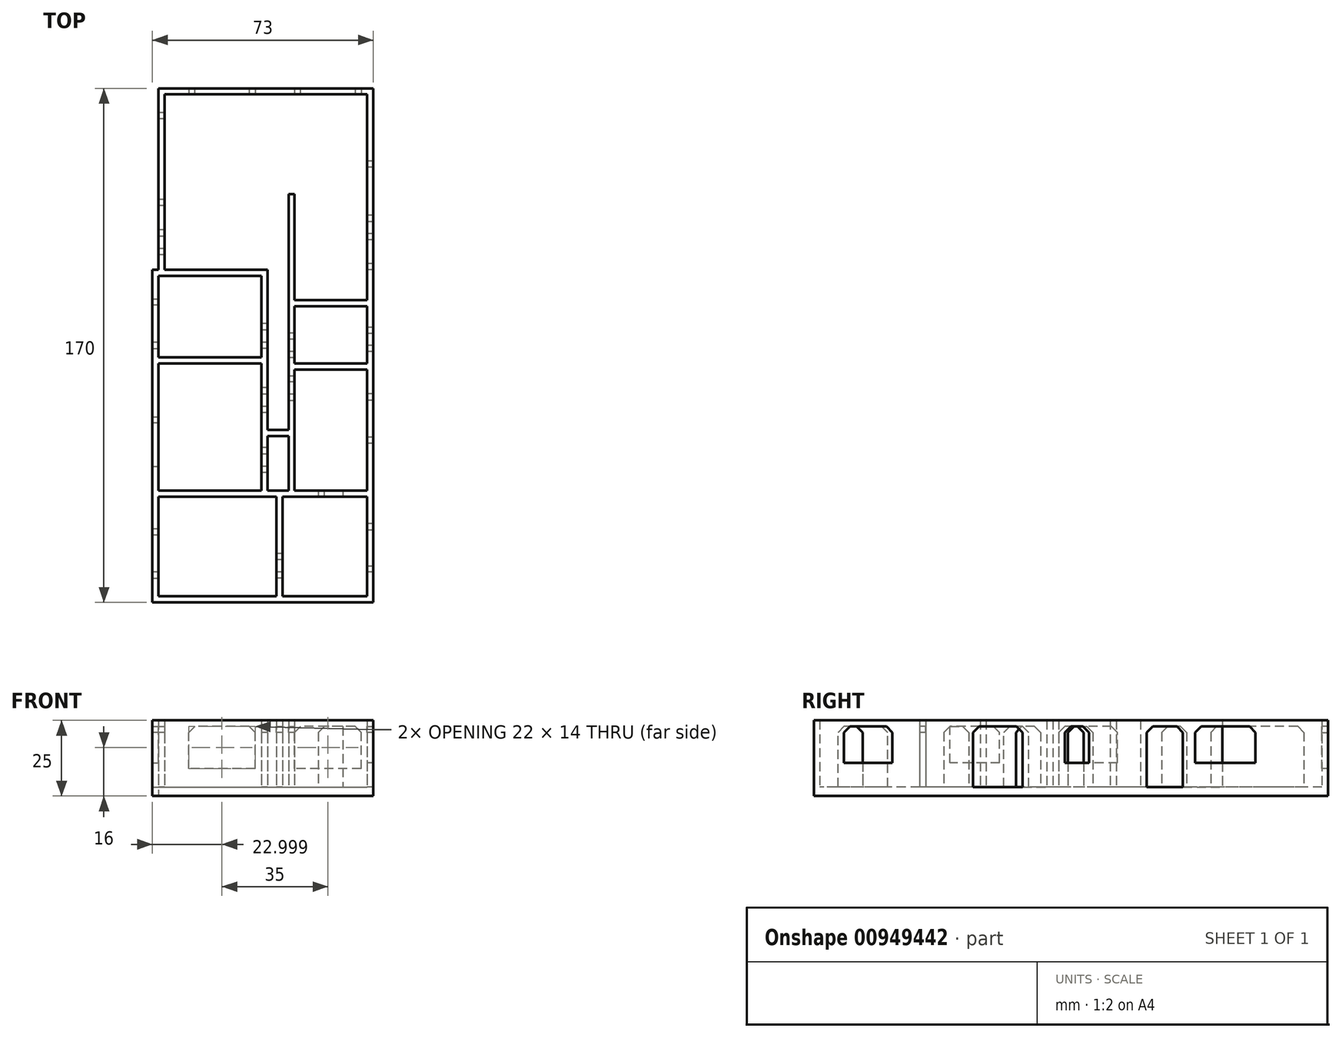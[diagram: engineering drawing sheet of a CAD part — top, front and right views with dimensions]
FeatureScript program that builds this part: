
annotation { "Feature Type Name" : "Feature", "Feature Type Description" : "" }
export const myFeature = defineFeature(function(context is Context, id is Id, definition is map)
    precondition{}
    {
        {
            assignVariable(context, id + "F0", {"name" : "WallWidth", "anyValue" : 2});
        }
        {
            assignVariable(context, id + "F1", {"name" : "Floor", "anyValue" : 3});
        }
        {
            assignVariable(context, id + "F2", {"name" : "DoorC", "anyValue" : 2});
        }
        {
            var Q0;
            Q0=qCreatedBy(makeId("Top.planeOp"),FACE);
            var sketch = newSketch(context, id + "F3", { "sketchPlane" : qUnion([Q0])});
            skLineSegment(sketch, "E0.bottom", {"start": v(-13.18, 167.27) * mm, "end": v(57.82, 167.27) * mm});
            skLineSegment(sketch, "E0.top", {"start": v(-13.18, -2.73) * mm, "end": v(57.82, -2.73) * mm});
            skLineSegment(sketch, "E0.left", {"start": v(-13.18, 167.27) * mm, "end": v(-13.18, -2.73) * mm});
            skLineSegment(sketch, "E0.right", {"start": v(57.82, 167.27) * mm, "end": v(57.82, -2.73) * mm});
            skLineSegment(sketch, "E1.bottom", {"start": v(-13.18, -2.73) * mm, "end": v(-15.18, -2.73) * mm});
            skLineSegment(sketch, "E1.top", {"start": v(-13.18, 107.27) * mm, "end": v(-15.18, 107.27) * mm});
            skLineSegment(sketch, "E1.left", {"start": v(-13.18, -2.73) * mm, "end": v(-13.18, 107.27) * mm});
            skLineSegment(sketch, "E1.right", {"start": v(-15.18, -2.73) * mm, "end": v(-15.18, 107.27) * mm});
            skSolve(sketch);
        }
        {
            var Q0;
            Q0 = qSketchRegion(id + "F3", true);
            extrude(context, id + "F4", {"entities" : qUnion([Q0]), "depth" : (getVariable(context, 'Floor')) * mm, "offsetDistance" : 25 * mm});
        }
        {
            var Q0;
            Q0=makeQuery(id+"F4.opExtrude","CAP_FACE",FACE,{"disambiguationData":[OSD([sQuery(id+"F3.wireOp",EDGE,"E0.bottom"),sQuery(id+"F3.wireOp",EDGE,"E0.top"),sQuery(id+"F3.wireOp",EDGE,"E0.left"),sQuery(id+"F3.wireOp",EDGE,"E0.right"),sQuery(id+"F3.wireOp",EDGE,"E1.bottom"),sQuery(id+"F3.wireOp",EDGE,"E1.top"),sQuery(id+"F3.wireOp",EDGE,"E1.right")])],"isStart":false});
            var sketch = newSketch(context, id + "F5", { "sketchPlane" : qUnion([Q0])});
            skLineSegment(sketch, "E2.bottom", {"start": v(-15.18, -2.73) * mm, "end": v(57.82, -2.73) * mm});
            skLineSegment(sketch, "E2.top", {"start": v(-15.18, -0.73) * mm, "end": v(57.82, -0.73) * mm});
            skLineSegment(sketch, "E2.left", {"start": v(-15.18, -2.73) * mm, "end": v(-15.18, -0.73) * mm});
            skLineSegment(sketch, "E2.right", {"start": v(57.82, -2.73) * mm, "end": v(57.82, -0.73) * mm});
            skLineSegment(sketch, "E3.bottom", {"start": v(25.82, 32.27) * mm, "end": v(27.82, 32.27) * mm});
            skLineSegment(sketch, "E3.top", {"start": v(25.82, -0.73) * mm, "end": v(27.82, -0.73) * mm});
            skLineSegment(sketch, "E3.left", {"start": v(25.82, 32.27) * mm, "end": v(25.82, -0.73) * mm});
            skLineSegment(sketch, "E3.right", {"start": v(27.82, 32.27) * mm, "end": v(27.82, -0.73) * mm});
            skLineSegment(sketch, "E4.bottom", {"start": v(-15.18, 107.27) * mm, "end": v(-13.18, 107.27) * mm});
            skLineSegment(sketch, "E4.top", {"start": v(-15.18, -0.73) * mm, "end": v(-13.18, -0.73) * mm});
            skLineSegment(sketch, "E4.left", {"start": v(-15.18, 107.27) * mm, "end": v(-15.18, -0.73) * mm});
            skLineSegment(sketch, "E4.right", {"start": v(-13.18, 107.27) * mm, "end": v(-13.18, -0.73) * mm});
            skLineSegment(sketch, "E5.bottom", {"start": v(55.82, 32.27) * mm, "end": v(57.82, 32.27) * mm});
            skLineSegment(sketch, "E5.top", {"start": v(55.82, -0.73) * mm, "end": v(57.82, -0.73) * mm});
            skLineSegment(sketch, "E5.left", {"start": v(55.82, 32.27) * mm, "end": v(55.82, -0.73) * mm});
            skLineSegment(sketch, "E5.right", {"start": v(57.82, 32.27) * mm, "end": v(57.82, -0.73) * mm});
            skLineSegment(sketch, "E6.bottom", {"start": v(-13.18, 34.27) * mm, "end": v(57.82, 34.27) * mm});
            skLineSegment(sketch, "E6.top", {"start": v(-13.18, 32.27) * mm, "end": v(57.82, 32.27) * mm});
            skLineSegment(sketch, "E6.left", {"start": v(-13.18, 34.27) * mm, "end": v(-13.18, 32.27) * mm});
            skLineSegment(sketch, "E6.right", {"start": v(57.82, 34.27) * mm, "end": v(57.82, 32.27) * mm});
            skLineSegment(sketch, "E7.bottom", {"start": v(55.82, 34.27) * mm, "end": v(57.82, 34.27) * mm});
            skLineSegment(sketch, "E7.top", {"start": v(55.82, 74.27) * mm, "end": v(57.82, 74.27) * mm});
            skLineSegment(sketch, "E7.left", {"start": v(55.82, 34.27) * mm, "end": v(55.82, 74.27) * mm});
            skLineSegment(sketch, "E7.right", {"start": v(57.82, 34.27) * mm, "end": v(57.82, 74.27) * mm});
            skLineSegment(sketch, "E8.bottom", {"start": v(29.82, 76.27) * mm, "end": v(57.82, 76.27) * mm});
            skLineSegment(sketch, "E8.top", {"start": v(29.82, 74.27) * mm, "end": v(57.82, 74.27) * mm});
            skLineSegment(sketch, "E8.left", {"start": v(29.82, 76.27) * mm, "end": v(29.82, 74.27) * mm});
            skLineSegment(sketch, "E8.right", {"start": v(57.82, 76.27) * mm, "end": v(57.82, 74.27) * mm});
            skLineSegment(sketch, "E9.bottom", {"start": v(-13.18, 78.27) * mm, "end": v(22.82, 78.27) * mm});
            skLineSegment(sketch, "E9.top", {"start": v(-13.18, 76.27) * mm, "end": v(22.82, 76.27) * mm});
            skLineSegment(sketch, "E9.left", {"start": v(-13.18, 78.27) * mm, "end": v(-13.18, 76.27) * mm});
            skLineSegment(sketch, "E9.right", {"start": v(22.82, 78.27) * mm, "end": v(22.82, 76.27) * mm});
            skLineSegment(sketch, "E10.bottom", {"start": v(22.82, 76.27) * mm, "end": v(20.82, 76.27) * mm});
            skLineSegment(sketch, "E10.top", {"start": v(22.82, 34.27) * mm, "end": v(20.82, 34.27) * mm});
            skLineSegment(sketch, "E10.left", {"start": v(22.82, 76.27) * mm, "end": v(22.82, 34.27) * mm});
            skLineSegment(sketch, "E10.right", {"start": v(20.82, 76.27) * mm, "end": v(20.82, 34.27) * mm});
            skLineSegment(sketch, "E11.bottom", {"start": v(29.82, 74.27) * mm, "end": v(31.82, 74.27) * mm});
            skLineSegment(sketch, "E11.top", {"start": v(29.82, 34.27) * mm, "end": v(31.82, 34.27) * mm});
            skLineSegment(sketch, "E11.left", {"start": v(29.82, 74.27) * mm, "end": v(29.82, 34.27) * mm});
            skLineSegment(sketch, "E11.right", {"start": v(31.82, 74.27) * mm, "end": v(31.82, 34.27) * mm});
            skLineSegment(sketch, "E12.bottom", {"start": v(-13.18, 107.27) * mm, "end": v(22.82, 107.27) * mm});
            skLineSegment(sketch, "E12.top", {"start": v(-13.18, 105.27) * mm, "end": v(22.82, 105.27) * mm});
            skLineSegment(sketch, "E12.left", {"start": v(-13.18, 107.27) * mm, "end": v(-13.18, 105.27) * mm});
            skLineSegment(sketch, "E12.right", {"start": v(22.82, 107.27) * mm, "end": v(22.82, 105.27) * mm});
            skLineSegment(sketch, "E13.bottom", {"start": v(22.82, 105.27) * mm, "end": v(20.82, 105.27) * mm});
            skLineSegment(sketch, "E13.top", {"start": v(22.82, 78.27) * mm, "end": v(20.82, 78.27) * mm});
            skLineSegment(sketch, "E13.left", {"start": v(22.82, 105.27) * mm, "end": v(22.82, 78.27) * mm});
            skLineSegment(sketch, "E13.right", {"start": v(20.82, 105.27) * mm, "end": v(20.82, 78.27) * mm});
            skLineSegment(sketch, "E14.bottom", {"start": v(-13.18, 167.27) * mm, "end": v(-11.18, 167.27) * mm});
            skLineSegment(sketch, "E14.top", {"start": v(-13.18, 107.27) * mm, "end": v(-11.18, 107.27) * mm});
            skLineSegment(sketch, "E14.left", {"start": v(-13.18, 167.27) * mm, "end": v(-13.18, 107.27) * mm});
            skLineSegment(sketch, "E14.right", {"start": v(-11.18, 167.27) * mm, "end": v(-11.18, 107.27) * mm});
            skLineSegment(sketch, "E15.bottom", {"start": v(-11.18, 167.27) * mm, "end": v(57.82, 167.27) * mm});
            skLineSegment(sketch, "E15.top", {"start": v(-11.18, 165.27) * mm, "end": v(57.82, 165.27) * mm});
            skLineSegment(sketch, "E15.left", {"start": v(-11.18, 167.27) * mm, "end": v(-11.18, 165.27) * mm});
            skLineSegment(sketch, "E15.right", {"start": v(57.82, 167.27) * mm, "end": v(57.82, 165.27) * mm});
            skLineSegment(sketch, "E16.bottom", {"start": v(57.82, 165.27) * mm, "end": v(55.82, 165.27) * mm});
            skLineSegment(sketch, "E16.top", {"start": v(57.82, 76.27) * mm, "end": v(55.82, 76.27) * mm});
            skLineSegment(sketch, "E16.left", {"start": v(57.82, 165.27) * mm, "end": v(57.82, 76.27) * mm});
            skLineSegment(sketch, "E16.right", {"start": v(55.82, 165.27) * mm, "end": v(55.82, 76.27) * mm});
            skLineSegment(sketch, "E17.bottom", {"start": v(29.82, 97.27) * mm, "end": v(55.82, 97.27) * mm});
            skLineSegment(sketch, "E17.top", {"start": v(29.82, 95.27) * mm, "end": v(55.82, 95.27) * mm});
            skLineSegment(sketch, "E17.left", {"start": v(29.82, 97.27) * mm, "end": v(29.82, 95.27) * mm});
            skLineSegment(sketch, "E17.right", {"start": v(55.82, 97.27) * mm, "end": v(55.82, 95.27) * mm});
            skLineSegment(sketch, "E18.bottom", {"start": v(29.82, 97.27) * mm, "end": v(31.82, 97.27) * mm});
            skLineSegment(sketch, "E18.top", {"start": v(29.82, 132.27) * mm, "end": v(31.82, 132.27) * mm});
            skLineSegment(sketch, "E18.left", {"start": v(29.82, 97.27) * mm, "end": v(29.82, 132.27) * mm});
            skLineSegment(sketch, "E18.right", {"start": v(31.82, 97.27) * mm, "end": v(31.82, 132.27) * mm});
            skLineSegment(sketch, "E19.bottom", {"start": v(29.82, 95.27) * mm, "end": v(31.82, 95.27) * mm});
            skLineSegment(sketch, "E19.top", {"start": v(29.82, 76.27) * mm, "end": v(31.82, 76.27) * mm});
            skLineSegment(sketch, "E19.left", {"start": v(29.82, 95.27) * mm, "end": v(29.82, 76.27) * mm});
            skLineSegment(sketch, "E19.right", {"start": v(31.82, 95.27) * mm, "end": v(31.82, 76.27) * mm});
            skLineSegment(sketch, "E20.bottom", {"start": v(22.82, 52.27) * mm, "end": v(29.82, 52.27) * mm});
            skLineSegment(sketch, "E20.top", {"start": v(22.82, 54.27) * mm, "end": v(29.82, 54.27) * mm});
            skLineSegment(sketch, "E20.left", {"start": v(22.82, 52.27) * mm, "end": v(22.82, 54.27) * mm});
            skLineSegment(sketch, "E20.right", {"start": v(29.82, 52.27) * mm, "end": v(29.82, 54.27) * mm});
            skSolve(sketch);
        }
        {
            var Q0;
            {var subQ2=sQuery(id+"F5.wireOp",EDGE,"E3.bottom");var subQ19=sQuery(id+"F5.wireOp",EDGE,"E5.bottom");var subQ20=makeQuery(id+"F5.imprint","IMPRINT",EDGE,{"derivedFrom":subQ19});var subQ23=sQuery(id+"F5.wireOp",EDGE,"E16.left");var subQ31=sQuery(id+"F5.wireOp",EDGE,"E7.top");var subQ32=makeQuery(id+"F5.imprint","IMPRINT",EDGE,{"derivedFrom":subQ31});var subQ37=sQuery(id+"F5.wireOp",EDGE,"E4.bottom");var subQ59=sQuery(id+"F5.wireOp",EDGE,"E12.right");var subQ67=sQuery(id+"F5.wireOp",EDGE,"E15.bottom");var subQ68=sQuery(id+"F5.wireOp",EDGE,"E14.bottom");Q0=qUnion([makeQuery(id+"F5.imprint","IMPRINT",FACE,{"disambiguationData":[TD([[subQ20,-1.0]])]}),makeQuery(id+"F5.imprint","IMPRINT",FACE,{"disambiguationData":[TD([[subQ32,-1.0]])]}),makeQuery(id+"F5.imprint","IMPRINT",FACE,{"disambiguationData":[TD([[makeQuery(id+"F5.imprint","IMPRINT",EDGE,{"derivedFrom":subQ68}),-1.0]])]}),makeQuery(id+"F5.imprint","IMPRINT",FACE,{"disambiguationData":[TD([[makeQuery(id+"F5.imprint","IMPRINT",EDGE,{"derivedFrom":subQ67}),-1.0]])]}),makeQuery(id+"F5.imprint","IMPRINT",FACE,{"disambiguationData":[TD([[makeQuery(id+"F5.imprint","IMPRINT",EDGE,{"derivedFrom":sQuery(id+"F5.wireOp",EDGE,"E2.bottom")}),1.0]])]}),makeQuery(id+"F5.imprint","IMPRINT",FACE,{"disambiguationData":[TD([[makeQuery(id+"F5.imprint","IMPRINT",EDGE,{"derivedFrom":subQ59}),-1.0]])]}),makeQuery(id+"F5.imprint","IMPRINT",FACE,{"disambiguationData":[TD([[makeQuery(id+"F5.imprint","IMPRINT",EDGE,{"derivedFrom":subQ23}),-1.0]])]}),makeQuery(id+"F5.imprint","IMPRINT",FACE,{"disambiguationData":[TD([[makeQuery(id+"F5.imprint","IMPRINT",EDGE,{"derivedFrom":subQ37}),1.0]])]}),makeQuery(id+"F5.imprint","IMPRINT",FACE,{"disambiguationData":[TD([[subQ32,1.0]])]}),makeQuery(id+"F5.imprint","IMPRINT",FACE,{"disambiguationData":[TD([[makeQuery(id+"F5.imprint","IMPRINT",EDGE,{"derivedFrom":subQ2}),1.0]])]})]);}
            var Q1;
            {var subQ0=sQuery(id+"F5.wireOp",EDGE,"E13.left");Q1=makeQuery(id+"F5.imprint","IMPRINT",FACE,{"disambiguationData":[TD([[makeQuery(id+"F5.imprint","IMPRINT",EDGE,{"derivedFrom":subQ0}),-1.0]])]});}
            var Q2;
            {var subQ4=sQuery(id+"F5.wireOp",EDGE,"E10.right");Q2=makeQuery(id+"F5.imprint","IMPRINT",FACE,{"disambiguationData":[TD([[makeQuery(id+"F5.imprint","IMPRINT",EDGE,{"derivedFrom":subQ4}),1.0]])]});}
            var Q3;
            {var subQ7=sQuery(id+"F5.wireOp",EDGE,"E9.right");Q3=makeQuery(id+"F5.imprint","IMPRINT",FACE,{"disambiguationData":[TD([[makeQuery(id+"F5.imprint","IMPRINT",EDGE,{"derivedFrom":subQ7}),-1.0]])]});}
            var Q4;
            {var subQ2=sQuery(id+"F5.wireOp",EDGE,"E19.left");Q4=makeQuery(id+"F5.imprint","IMPRINT",FACE,{"disambiguationData":[TD([[makeQuery(id+"F5.imprint","IMPRINT",EDGE,{"derivedFrom":subQ2}),1.0]])]});}
            var Q5;
            {var subQ6=sQuery(id+"F5.wireOp",EDGE,"E17.left");Q5=makeQuery(id+"F5.imprint","IMPRINT",FACE,{"disambiguationData":[TD([[makeQuery(id+"F5.imprint","IMPRINT",EDGE,{"derivedFrom":subQ6}),1.0]])]});}
            var Q6;
            Q6=makeQuery(id+"F5.imprint","IMPRINT",FACE,{"disambiguationData":[TD([[makeQuery(id+"F5.imprint","IMPRINT",EDGE,{"derivedFrom":sQuery(id+"F5.wireOp",EDGE,"E18.top")}),-1.0]])]});
            var Q7;
            {var subQ4=sQuery(id+"F5.wireOp",EDGE,"E11.right");Q7=makeQuery(id+"F5.imprint","IMPRINT",FACE,{"disambiguationData":[TD([[makeQuery(id+"F5.imprint","IMPRINT",EDGE,{"derivedFrom":subQ4}),-1.0]])]});}
            var Q8;
            {var subQ0=sQuery(id+"F5.wireOp",EDGE,"E20.bottom");Q8=makeQuery(id+"F5.imprint","IMPRINT",FACE,{"disambiguationData":[TD([[makeQuery(id+"F5.imprint","IMPRINT",EDGE,{"derivedFrom":subQ0}),1.0]])]});}
            var Q9;
            Q9=makeQuery(id+"F5.imprint","IMPRINT",FACE,{"disambiguationData":[TD([[makeQuery(id+"F5.imprint","IMPRINT",EDGE,{"derivedFrom":sQuery(id+"F5.wireOp",EDGE,"E3.bottom")}),-1.0]])]});
            extrude(context, id + "F6", {"entities" : qUnion([Q0, Q1, Q2, Q3, Q4, Q5, Q6, Q7, Q8, Q9]), "operationType" : NewBodyOperationType.ADD, "depth" : (20 + getVariable(context, 'DoorC')) * mm, "offsetDistance" : 25 * mm});
        }
        {
            var Q0;
            Q0=makeQuery(id+"F6.boolean.opBoolean","MERGE",FACE,{"derivedFrom":[makeQuery(id+"F4.opExtrude","SWEPT_FACE",FACE,{"disambiguationData":[OSD([sQuery(id+"F3.wireOp",EDGE,"E0.left")])]}),makeQuery(id+"F6.opExtrude","SWEPT_FACE",FACE,{"disambiguationData":[OSD([sQuery(id+"F5.wireOp",EDGE,"E14.left")])]})]});
            var sketch = newSketch(context, id + "F7", { "sketchPlane" : qUnion([Q0])});
            skLineSegment(sketch, "E21.bottom", {"start": v(-120.47, 23) * mm, "end": v(-112.27, 23) * mm});
            skLineSegment(sketch, "E21.top", {"start": v(-120.47, 3) * mm, "end": v(-112.27, 3) * mm});
            skLineSegment(sketch, "E21.left", {"start": v(-120.47, 23) * mm, "end": v(-120.47, 3) * mm});
            skLineSegment(sketch, "E21.right", {"start": v(-112.27, 23) * mm, "end": v(-112.27, 3) * mm});
            skLineSegment(sketch, "E22.bottom", {"start": v(-159.27, 23) * mm, "end": v(-128.47, 23) * mm});
            skLineSegment(sketch, "E22.top", {"start": v(-159.27, 3) * mm, "end": v(-128.47, 3) * mm});
            skLineSegment(sketch, "E22.left", {"start": v(-159.27, 23) * mm, "end": v(-159.27, 3) * mm});
            skLineSegment(sketch, "E22.right", {"start": v(-128.47, 23) * mm, "end": v(-128.47, 3) * mm});
            skSolve(sketch);
        }
        {
            var Q0;
            Q0 = qSketchRegion(id + "F7", true);
            extrude(context, id + "F8", {"entities" : qUnion([Q0]), "operationType" : NewBodyOperationType.REMOVE, "oppositeDirection" : true, "depth" : (getVariable(context, 'WallWidth')) * mm, "offsetDistance" : 25 * mm});
        }
        {
            var Q0;
            {var subQ0=sQuery(id+"F5.wireOp",EDGE,"E16.right");Q0=makeQuery(id+"F6.opExtrude","SWEPT_FACE",FACE,{"disambiguationData":[OSD([subQ0]),TDD([makeQuery(id+"F5.imprint","IMPRINT",EDGE,{"disambiguationData":[TD([[makeQuery(id+"F5.imprint","INTERSECT",VERTEX,{"derivedFrom":[sQuery(id+"F5.wireOp",EDGE,"E15.top"),subQ0]}),-1.0]])],"derivedFrom":subQ0})])]});}
            var sketch = newSketch(context, id + "F9", { "sketchPlane" : qUnion([Q0])});
            skLineSegment(sketch, "E23.bottom", {"start": v(-107.27, 23) * mm, "end": v(-119.27, 23) * mm});
            skLineSegment(sketch, "E23.top", {"start": v(-107.27, 3) * mm, "end": v(-119.27, 3) * mm});
            skLineSegment(sketch, "E23.left", {"start": v(-107.27, 23) * mm, "end": v(-107.27, 3) * mm});
            skLineSegment(sketch, "E23.right", {"start": v(-119.27, 23) * mm, "end": v(-119.27, 3) * mm});
            skLineSegment(sketch, "E24.bottom", {"start": v(-123.27, 23) * mm, "end": v(-143.27, 23) * mm});
            skLineSegment(sketch, "E24.top", {"start": v(-123.27, 11) * mm, "end": v(-143.27, 11) * mm});
            skLineSegment(sketch, "E24.left", {"start": v(-123.27, 23) * mm, "end": v(-123.27, 11) * mm});
            skLineSegment(sketch, "E24.right", {"start": v(-143.27, 23) * mm, "end": v(-143.27, 11) * mm});
            skLineSegment(sketch, "E25.bottom", {"start": v(-88.27, 23) * mm, "end": v(-80.27, 23) * mm});
            skLineSegment(sketch, "E25.top", {"start": v(-88.27, 11) * mm, "end": v(-80.27, 11) * mm});
            skLineSegment(sketch, "E25.left", {"start": v(-88.27, 23) * mm, "end": v(-88.27, 11) * mm});
            skLineSegment(sketch, "E25.right", {"start": v(-80.27, 23) * mm, "end": v(-80.27, 11) * mm});
            skLineSegment(sketch, "E26.bottom", {"start": v(-66.27, 23) * mm, "end": v(-49.87, 23) * mm});
            skLineSegment(sketch, "E26.top", {"start": v(-66.27, 3) * mm, "end": v(-49.87, 3) * mm});
            skLineSegment(sketch, "E26.left", {"start": v(-66.27, 23) * mm, "end": v(-66.27, 3) * mm});
            skLineSegment(sketch, "E26.right", {"start": v(-49.87, 23) * mm, "end": v(-49.87, 3) * mm});
            skLineSegment(sketch, "E27.bottom", {"start": v(-23.27, 23) * mm, "end": v(-7.27, 23) * mm});
            skLineSegment(sketch, "E27.top", {"start": v(-23.27, 11) * mm, "end": v(-7.27, 11) * mm});
            skLineSegment(sketch, "E27.left", {"start": v(-23.27, 23) * mm, "end": v(-23.27, 11) * mm});
            skLineSegment(sketch, "E27.right", {"start": v(-7.27, 23) * mm, "end": v(-7.27, 11) * mm});
            skSolve(sketch);
        }
        {
            var Q0;
            Q0 = qSketchRegion(id + "F9", true);
            extrude(context, id + "F10", {"entities" : qUnion([Q0]), "operationType" : NewBodyOperationType.REMOVE, "oppositeDirection" : true, "depth" : (getVariable(context, 'WallWidth')) * mm, "offsetDistance" : 25 * mm});
        }
        {
            var Q0;
            Q0=makeQuery(id+"F6.opExtrude","SWEPT_FACE",FACE,{"disambiguationData":[OSD([sQuery(id+"F5.wireOp",EDGE,"E15.top")])]});
            var sketch = newSketch(context, id + "F11", { "sketchPlane" : qUnion([Q0])});
            skLineSegment(sketch, "E28.bottom", {"start": v(53.82, 9) * mm, "end": v(31.82, 9) * mm});
            skLineSegment(sketch, "E28.top", {"start": v(53.82, 23) * mm, "end": v(31.82, 23) * mm});
            skLineSegment(sketch, "E28.left", {"start": v(53.82, 9) * mm, "end": v(53.82, 23) * mm});
            skLineSegment(sketch, "E28.right", {"start": v(31.82, 9) * mm, "end": v(31.82, 23) * mm});
            skLineSegment(sketch, "E29.bottom", {"start": v(18.82, 9) * mm, "end": v(-3.18, 9) * mm});
            skLineSegment(sketch, "E29.top", {"start": v(18.82, 23) * mm, "end": v(-3.18, 23) * mm});
            skLineSegment(sketch, "E29.left", {"start": v(18.82, 9) * mm, "end": v(18.82, 23) * mm});
            skLineSegment(sketch, "E29.right", {"start": v(-3.18, 9) * mm, "end": v(-3.18, 23) * mm});
            skSolve(sketch);
        }
        {
            var Q0;
            Q0 = qSketchRegion(id + "F11", true);
            extrude(context, id + "F12", {"entities" : qUnion([Q0]), "operationType" : NewBodyOperationType.REMOVE, "oppositeDirection" : true, "depth" : (getVariable(context, 'WallWidth')) * mm, "offsetDistance" : 25 * mm});
        }
        {
            var Q0;
            Q0=makeQuery(id+"F6.opExtrude","SWEPT_FACE",FACE,{"disambiguationData":[OSD([sQuery(id+"F5.wireOp",EDGE,"E13.right")])]});
            var sketch = newSketch(context, id + "F13", { "sketchPlane" : qUnion([Q0])});
            skLineSegment(sketch, "E30.bottom", {"start": v(-81.27, 23) * mm, "end": v(-89.47, 23) * mm});
            skLineSegment(sketch, "E30.top", {"start": v(-81.27, 3) * mm, "end": v(-89.47, 3) * mm});
            skLineSegment(sketch, "E30.left", {"start": v(-81.27, 23) * mm, "end": v(-81.27, 3) * mm});
            skLineSegment(sketch, "E30.right", {"start": v(-89.47, 23) * mm, "end": v(-89.47, 3) * mm});
            skLineSegment(sketch, "E31.bottom", {"start": v(-68.27, 3) * mm, "end": v(-60.07, 3) * mm});
            skLineSegment(sketch, "E31.top", {"start": v(-68.27, 23) * mm, "end": v(-60.07, 23) * mm});
            skLineSegment(sketch, "E31.left", {"start": v(-68.27, 3) * mm, "end": v(-68.27, 23) * mm});
            skLineSegment(sketch, "E31.right", {"start": v(-60.07, 3) * mm, "end": v(-60.07, 23) * mm});
            skLineSegment(sketch, "E32.bottom", {"start": v(-40.27, 23) * mm, "end": v(-48.47, 23) * mm});
            skLineSegment(sketch, "E32.top", {"start": v(-40.27, 3) * mm, "end": v(-48.47, 3) * mm});
            skLineSegment(sketch, "E32.left", {"start": v(-40.27, 23) * mm, "end": v(-40.27, 3) * mm});
            skLineSegment(sketch, "E32.right", {"start": v(-48.47, 23) * mm, "end": v(-48.47, 3) * mm});
            skSolve(sketch);
        }
        {
            var Q0;
            Q0 = qSketchRegion(id + "F13", true);
            extrude(context, id + "F14", {"entities" : qUnion([Q0]), "operationType" : NewBodyOperationType.REMOVE, "oppositeDirection" : true, "depth" : (getVariable(context, 'WallWidth')) * mm, "offsetDistance" : 25 * mm});
        }
        {
            var Q0;
            Q0=makeQuery(id+"F6.opExtrude","SWEPT_FACE",FACE,{"disambiguationData":[OSD([sQuery(id+"F5.wireOp",EDGE,"E11.right")])]});
            var sketch = newSketch(context, id + "F15", { "sketchPlane" : qUnion([Q0])});
            skLineSegment(sketch, "E33.bottom", {"start": v(86.47, 23) * mm, "end": v(78.27, 23) * mm});
            skLineSegment(sketch, "E33.top", {"start": v(86.47, 3) * mm, "end": v(78.27, 3) * mm});
            skLineSegment(sketch, "E33.left", {"start": v(86.47, 23) * mm, "end": v(86.47, 3) * mm});
            skLineSegment(sketch, "E33.right", {"start": v(78.27, 23) * mm, "end": v(78.27, 3) * mm});
            skLineSegment(sketch, "E34.bottom", {"start": v(72.27, 23) * mm, "end": v(64.07, 23) * mm});
            skLineSegment(sketch, "E34.top", {"start": v(72.27, 3) * mm, "end": v(64.07, 3) * mm});
            skLineSegment(sketch, "E34.left", {"start": v(72.27, 23) * mm, "end": v(72.27, 3) * mm});
            skLineSegment(sketch, "E34.right", {"start": v(64.07, 23) * mm, "end": v(64.07, 3) * mm});
            skSolve(sketch);
        }
        {
            var Q0;
            Q0 = qSketchRegion(id + "F15", true);
            extrude(context, id + "F16", {"entities" : qUnion([Q0]), "operationType" : NewBodyOperationType.REMOVE, "oppositeDirection" : true, "depth" : (getVariable(context, 'WallWidth')) * mm, "offsetDistance" : 25 * mm});
        }
        {
            var Q0;
            {var subQ0=sQuery(id+"F5.wireOp",EDGE,"E6.top");Q0=makeQuery(id+"F6.opExtrude","SWEPT_FACE",FACE,{"disambiguationData":[OSD([subQ0]),TDD([makeQuery(id+"F5.imprint","IMPRINT",EDGE,{"disambiguationData":[TD([[makeQuery(id+"F5.imprint","INTERSECT",VERTEX,{"derivedFrom":[sQuery(id+"F5.wireOp",EDGE,"E3.bottom"),sQuery(id+"F5.wireOp",EDGE,"E3.right"),subQ0]}),-1.0]])],"derivedFrom":subQ0})])]});}
            var sketch = newSketch(context, id + "F17", { "sketchPlane" : qUnion([Q0])});
            skLineSegment(sketch, "E35.bottom", {"start": v(47.82, 23) * mm, "end": v(39.62, 23) * mm});
            skLineSegment(sketch, "E35.top", {"start": v(47.82, 3) * mm, "end": v(39.62, 3) * mm});
            skLineSegment(sketch, "E35.left", {"start": v(47.82, 23) * mm, "end": v(47.82, 3) * mm});
            skLineSegment(sketch, "E35.right", {"start": v(39.62, 23) * mm, "end": v(39.62, 3) * mm});
            skSolve(sketch);
        }
        {
            var Q0;
            Q0=makeQuery(id+"F17.imprint","IMPRINT",FACE,{"disambiguationData":[TD([[makeQuery(id+"F17.imprint","IMPRINT",EDGE,{"derivedFrom":sQuery(id+"F17.wireOp",EDGE,"E35.bottom")}),1.0]])]});
            extrude(context, id + "F18", {"entities" : qUnion([Q0]), "operationType" : NewBodyOperationType.REMOVE, "oppositeDirection" : true, "depth" : getVariable(context, 'WallWidth') * mm, "offsetDistance" : 25 * mm});
        }
        {
            var Q0;
            Q0=makeQuery(id+"F6.opExtrude","SWEPT_FACE",FACE,{"disambiguationData":[OSD([sQuery(id+"F5.wireOp",EDGE,"E3.left")])]});
            var sketch = newSketch(context, id + "F19", { "sketchPlane" : qUnion([Q0])});
            skLineSegment(sketch, "E36.bottom", {"start": v(-13.47, 23) * mm, "end": v(-5.27, 23) * mm});
            skLineSegment(sketch, "E36.top", {"start": v(-13.47, 3) * mm, "end": v(-5.27, 3) * mm});
            skLineSegment(sketch, "E36.left", {"start": v(-13.47, 23) * mm, "end": v(-13.47, 3) * mm});
            skLineSegment(sketch, "E36.right", {"start": v(-5.27, 23) * mm, "end": v(-5.27, 3) * mm});
            skSolve(sketch);
        }
        {
            var Q0;
            Q0 = qSketchRegion(id + "F19", true);
            extrude(context, id + "F20", {"entities" : qUnion([Q0]), "operationType" : NewBodyOperationType.REMOVE, "oppositeDirection" : true, "depth" : (getVariable(context, 'WallWidth')) * mm, "offsetDistance" : 25 * mm});
        }
        {
            var Q0;
            {var subQ0=sQuery(id+"F5.wireOp",EDGE,"E4.right");Q0=makeQuery(id+"F6.opExtrude","SWEPT_FACE",FACE,{"disambiguationData":[OSD([subQ0]),TDD([makeQuery(id+"F5.imprint","IMPRINT",EDGE,{"disambiguationData":[TD([[makeQuery(id+"F5.imprint","INTERSECT",VERTEX,{"derivedFrom":[sQuery(id+"F5.wireOp",EDGE,"E2.top"),subQ0]}),1.0]])],"derivedFrom":subQ0})])]});}
            var sketch = newSketch(context, id + "F21", { "sketchPlane" : qUnion([Q0])});
            skLineSegment(sketch, "E37.bottom", {"start": v(21.67, 3) * mm, "end": v(5.27, 3) * mm});
            skLineSegment(sketch, "E37.top", {"start": v(21.67, 23) * mm, "end": v(5.27, 23) * mm});
            skLineSegment(sketch, "E37.left", {"start": v(21.67, 3) * mm, "end": v(21.67, 23) * mm});
            skLineSegment(sketch, "E37.right", {"start": v(5.27, 3) * mm, "end": v(5.27, 23) * mm});
            skLineSegment(sketch, "E38.bottom", {"start": v(58.67, 11) * mm, "end": v(42.27, 11) * mm});
            skLineSegment(sketch, "E38.top", {"start": v(58.67, 23) * mm, "end": v(42.27, 23) * mm});
            skLineSegment(sketch, "E38.left", {"start": v(58.67, 11) * mm, "end": v(58.67, 23) * mm});
            skLineSegment(sketch, "E38.right", {"start": v(42.27, 11) * mm, "end": v(42.27, 23) * mm});
            skLineSegment(sketch, "E39.bottom", {"start": v(97.67, 11) * mm, "end": v(81.27, 11) * mm});
            skLineSegment(sketch, "E39.top", {"start": v(97.67, 23) * mm, "end": v(81.27, 23) * mm});
            skLineSegment(sketch, "E39.left", {"start": v(97.67, 11) * mm, "end": v(97.67, 23) * mm});
            skLineSegment(sketch, "E39.right", {"start": v(81.27, 11) * mm, "end": v(81.27, 23) * mm});
            skSolve(sketch);
        }
        {
            var Q0;
            Q0 = qSketchRegion(id + "F21", true);
            extrude(context, id + "F22", {"entities" : qUnion([Q0]), "operationType" : NewBodyOperationType.REMOVE, "oppositeDirection" : true, "depth" : (getVariable(context, 'WallWidth')) * mm, "offsetDistance" : 25 * mm});
        }
        {
            var Q0;
            Q0=makeQuery(id+"F8.boolean.opBoolean","COPY",EDGE,{"derivedFrom":makeQuery(id+"F8.opExtrude","SWEPT_EDGE",EDGE,{"disambiguationData":[OSD([sQuery(id+"F7.wireOp",EDGE,"E22.bottom"),sQuery(id+"F7.wireOp",EDGE,"E22.left")])]})});
            var Q1;
            Q1=makeQuery(id+"F8.boolean.opBoolean","COPY",EDGE,{"derivedFrom":makeQuery(id+"F8.opExtrude","SWEPT_EDGE",EDGE,{"disambiguationData":[OSD([sQuery(id+"F7.wireOp",EDGE,"E22.bottom"),sQuery(id+"F7.wireOp",EDGE,"E22.right")])]})});
            var Q2;
            Q2=makeQuery(id+"F8.boolean.opBoolean","COPY",EDGE,{"derivedFrom":makeQuery(id+"F8.opExtrude","SWEPT_EDGE",EDGE,{"disambiguationData":[OSD([sQuery(id+"F7.wireOp",EDGE,"E21.bottom"),sQuery(id+"F7.wireOp",EDGE,"E21.right")])]})});
            var Q3;
            Q3=makeQuery(id+"F22.boolean.opBoolean","COPY",EDGE,{"derivedFrom":makeQuery(id+"F22.opExtrude","SWEPT_EDGE",EDGE,{"disambiguationData":[OSD([sQuery(id+"F21.wireOp",EDGE,"E39.top"),sQuery(id+"F21.wireOp",EDGE,"E39.right")])]})});
            var Q4;
            Q4=makeQuery(id+"F12.boolean.opBoolean","COPY",EDGE,{"derivedFrom":makeQuery(id+"F12.opExtrude","SWEPT_EDGE",EDGE,{"disambiguationData":[OSD([sQuery(id+"F11.wireOp",EDGE,"E29.top"),sQuery(id+"F11.wireOp",EDGE,"E29.left")])]})});
            var Q5;
            Q5=makeQuery(id+"F22.boolean.opBoolean","COPY",EDGE,{"derivedFrom":makeQuery(id+"F22.opExtrude","SWEPT_EDGE",EDGE,{"disambiguationData":[OSD([sQuery(id+"F21.wireOp",EDGE,"E37.top"),sQuery(id+"F21.wireOp",EDGE,"E37.left")])]})});
            var Q6;
            Q6=makeQuery(id+"F22.boolean.opBoolean","COPY",EDGE,{"derivedFrom":makeQuery(id+"F22.opExtrude","SWEPT_EDGE",EDGE,{"disambiguationData":[OSD([sQuery(id+"F21.wireOp",EDGE,"E38.top"),sQuery(id+"F21.wireOp",EDGE,"E38.left")])]})});
            var Q7;
            Q7=makeQuery(id+"F22.boolean.opBoolean","COPY",EDGE,{"derivedFrom":makeQuery(id+"F22.opExtrude","SWEPT_EDGE",EDGE,{"disambiguationData":[OSD([sQuery(id+"F21.wireOp",EDGE,"E39.top"),sQuery(id+"F21.wireOp",EDGE,"E39.left")])]})});
            var Q8;
            Q8=makeQuery(id+"F8.boolean.opBoolean","COPY",EDGE,{"derivedFrom":makeQuery(id+"F8.opExtrude","SWEPT_EDGE",EDGE,{"disambiguationData":[OSD([sQuery(id+"F7.wireOp",EDGE,"E21.bottom"),sQuery(id+"F7.wireOp",EDGE,"E21.left")])]})});
            var Q9;
            Q9=makeQuery(id+"F22.boolean.opBoolean","COPY",EDGE,{"derivedFrom":makeQuery(id+"F22.opExtrude","SWEPT_EDGE",EDGE,{"disambiguationData":[OSD([sQuery(id+"F21.wireOp",EDGE,"E37.top"),sQuery(id+"F21.wireOp",EDGE,"E37.right")])]})});
            var Q10;
            Q10=makeQuery(id+"F10.boolean.opBoolean","COPY",EDGE,{"derivedFrom":makeQuery(id+"F10.opExtrude","SWEPT_EDGE",EDGE,{"disambiguationData":[OSD([sQuery(id+"F9.wireOp",EDGE,"E27.bottom"),sQuery(id+"F9.wireOp",EDGE,"E27.right")])]})});
            var Q11;
            Q11=makeQuery(id+"F20.boolean.opBoolean","COPY",EDGE,{"derivedFrom":makeQuery(id+"F20.opExtrude","SWEPT_EDGE",EDGE,{"disambiguationData":[OSD([sQuery(id+"F19.wireOp",EDGE,"E36.bottom"),sQuery(id+"F19.wireOp",EDGE,"E36.right")])]})});
            var Q12;
            Q12=makeQuery(id+"F10.boolean.opBoolean","COPY",EDGE,{"derivedFrom":makeQuery(id+"F10.opExtrude","SWEPT_EDGE",EDGE,{"disambiguationData":[OSD([sQuery(id+"F9.wireOp",EDGE,"E26.bottom"),sQuery(id+"F9.wireOp",EDGE,"E26.right")])]})});
            var Q13;
            Q13=makeQuery(id+"F10.boolean.opBoolean","COPY",EDGE,{"derivedFrom":makeQuery(id+"F10.opExtrude","SWEPT_EDGE",EDGE,{"disambiguationData":[OSD([sQuery(id+"F9.wireOp",EDGE,"E25.bottom"),sQuery(id+"F9.wireOp",EDGE,"E25.right")])]})});
            var Q14;
            Q14=makeQuery(id+"F10.boolean.opBoolean","COPY",EDGE,{"derivedFrom":makeQuery(id+"F10.opExtrude","SWEPT_EDGE",EDGE,{"disambiguationData":[OSD([sQuery(id+"F9.wireOp",EDGE,"E27.bottom"),sQuery(id+"F9.wireOp",EDGE,"E27.left")])]})});
            var Q15;
            Q15=makeQuery(id+"F10.boolean.opBoolean","COPY",EDGE,{"derivedFrom":makeQuery(id+"F10.opExtrude","SWEPT_EDGE",EDGE,{"disambiguationData":[OSD([sQuery(id+"F9.wireOp",EDGE,"E26.bottom"),sQuery(id+"F9.wireOp",EDGE,"E26.left")])]})});
            var Q16;
            Q16=makeQuery(id+"F10.boolean.opBoolean","COPY",EDGE,{"derivedFrom":makeQuery(id+"F10.opExtrude","SWEPT_EDGE",EDGE,{"disambiguationData":[OSD([sQuery(id+"F9.wireOp",EDGE,"E25.bottom"),sQuery(id+"F9.wireOp",EDGE,"E25.left")])]})});
            var Q17;
            Q17=makeQuery(id+"F18.boolean.opBoolean","COPY",EDGE,{"derivedFrom":makeQuery(id+"F18.opExtrude","SWEPT_EDGE",EDGE,{"disambiguationData":[OSD([sQuery(id+"F17.wireOp",EDGE,"E35.bottom"),sQuery(id+"F17.wireOp",EDGE,"E35.right")])]})});
            var Q18;
            Q18=makeQuery(id+"F16.boolean.opBoolean","COPY",EDGE,{"derivedFrom":makeQuery(id+"F16.opExtrude","SWEPT_EDGE",EDGE,{"disambiguationData":[OSD([sQuery(id+"F15.wireOp",EDGE,"E34.bottom"),sQuery(id+"F15.wireOp",EDGE,"E34.left")])]})});
            var Q19;
            Q19=makeQuery(id+"F14.boolean.opBoolean","COPY",EDGE,{"derivedFrom":makeQuery(id+"F14.opExtrude","SWEPT_EDGE",EDGE,{"disambiguationData":[OSD([sQuery(id+"F13.wireOp",EDGE,"E31.top"),sQuery(id+"F13.wireOp",EDGE,"E31.left")])]})});
            var Q20;
            Q20=makeQuery(id+"F20.boolean.opBoolean","COPY",EDGE,{"derivedFrom":makeQuery(id+"F20.opExtrude","SWEPT_EDGE",EDGE,{"disambiguationData":[OSD([sQuery(id+"F19.wireOp",EDGE,"E36.bottom"),sQuery(id+"F19.wireOp",EDGE,"E36.left")])]})});
            var Q21;
            Q21=makeQuery(id+"F12.boolean.opBoolean","COPY",EDGE,{"derivedFrom":makeQuery(id+"F12.opExtrude","SWEPT_EDGE",EDGE,{"disambiguationData":[OSD([sQuery(id+"F11.wireOp",EDGE,"E28.top"),sQuery(id+"F11.wireOp",EDGE,"E28.right")])]})});
            var Q22;
            Q22=makeQuery(id+"F10.boolean.opBoolean","COPY",EDGE,{"derivedFrom":makeQuery(id+"F10.opExtrude","SWEPT_EDGE",EDGE,{"disambiguationData":[OSD([sQuery(id+"F9.wireOp",EDGE,"E24.bottom"),sQuery(id+"F9.wireOp",EDGE,"E24.left")])]})});
            var Q23;
            Q23=makeQuery(id+"F10.boolean.opBoolean","COPY",EDGE,{"derivedFrom":makeQuery(id+"F10.opExtrude","SWEPT_EDGE",EDGE,{"disambiguationData":[OSD([sQuery(id+"F9.wireOp",EDGE,"E23.bottom"),sQuery(id+"F9.wireOp",EDGE,"E23.left")])]})});
            var Q24;
            Q24=makeQuery(id+"F10.boolean.opBoolean","COPY",EDGE,{"derivedFrom":makeQuery(id+"F10.opExtrude","SWEPT_EDGE",EDGE,{"disambiguationData":[OSD([sQuery(id+"F9.wireOp",EDGE,"E23.bottom"),sQuery(id+"F9.wireOp",EDGE,"E23.right")])]})});
            var Q25;
            Q25=makeQuery(id+"F10.boolean.opBoolean","COPY",EDGE,{"derivedFrom":makeQuery(id+"F10.opExtrude","SWEPT_EDGE",EDGE,{"disambiguationData":[OSD([sQuery(id+"F9.wireOp",EDGE,"E24.bottom"),sQuery(id+"F9.wireOp",EDGE,"E24.right")])]})});
            var Q26;
            Q26=makeQuery(id+"F12.boolean.opBoolean","COPY",EDGE,{"derivedFrom":makeQuery(id+"F12.opExtrude","SWEPT_EDGE",EDGE,{"disambiguationData":[OSD([sQuery(id+"F11.wireOp",EDGE,"E28.top"),sQuery(id+"F11.wireOp",EDGE,"E28.left")])]})});
            var Q27;
            Q27=makeQuery(id+"F12.boolean.opBoolean","COPY",EDGE,{"derivedFrom":makeQuery(id+"F12.opExtrude","SWEPT_EDGE",EDGE,{"disambiguationData":[OSD([sQuery(id+"F11.wireOp",EDGE,"E29.top"),sQuery(id+"F11.wireOp",EDGE,"E29.right")])]})});
            var Q28;
            Q28=makeQuery(id+"F16.boolean.opBoolean","COPY",EDGE,{"derivedFrom":makeQuery(id+"F16.opExtrude","SWEPT_EDGE",EDGE,{"disambiguationData":[OSD([sQuery(id+"F15.wireOp",EDGE,"E33.bottom"),sQuery(id+"F15.wireOp",EDGE,"E33.right")])]})});
            var Q29;
            Q29=makeQuery(id+"F16.boolean.opBoolean","COPY",EDGE,{"derivedFrom":makeQuery(id+"F16.opExtrude","SWEPT_EDGE",EDGE,{"disambiguationData":[OSD([sQuery(id+"F15.wireOp",EDGE,"E33.bottom"),sQuery(id+"F15.wireOp",EDGE,"E33.left")])]})});
            var Q30;
            Q30=makeQuery(id+"F16.boolean.opBoolean","COPY",EDGE,{"derivedFrom":makeQuery(id+"F16.opExtrude","SWEPT_EDGE",EDGE,{"disambiguationData":[OSD([sQuery(id+"F15.wireOp",EDGE,"E34.bottom"),sQuery(id+"F15.wireOp",EDGE,"E34.right")])]})});
            var Q31;
            Q31=makeQuery(id+"F14.boolean.opBoolean","COPY",EDGE,{"derivedFrom":makeQuery(id+"F14.opExtrude","SWEPT_EDGE",EDGE,{"disambiguationData":[OSD([sQuery(id+"F13.wireOp",EDGE,"E30.bottom"),sQuery(id+"F13.wireOp",EDGE,"E30.right")])]})});
            var Q32;
            Q32=makeQuery(id+"F14.boolean.opBoolean","COPY",EDGE,{"derivedFrom":makeQuery(id+"F14.opExtrude","SWEPT_EDGE",EDGE,{"disambiguationData":[OSD([sQuery(id+"F13.wireOp",EDGE,"E30.bottom"),sQuery(id+"F13.wireOp",EDGE,"E30.left")])]})});
            var Q33;
            Q33=makeQuery(id+"F14.boolean.opBoolean","COPY",EDGE,{"derivedFrom":makeQuery(id+"F14.opExtrude","SWEPT_EDGE",EDGE,{"disambiguationData":[OSD([sQuery(id+"F13.wireOp",EDGE,"E32.bottom"),sQuery(id+"F13.wireOp",EDGE,"E32.left")])]})});
            var Q34;
            Q34=makeQuery(id+"F14.boolean.opBoolean","COPY",EDGE,{"derivedFrom":makeQuery(id+"F14.opExtrude","SWEPT_EDGE",EDGE,{"disambiguationData":[OSD([sQuery(id+"F13.wireOp",EDGE,"E32.bottom"),sQuery(id+"F13.wireOp",EDGE,"E32.right")])]})});
            var Q35;
            Q35=makeQuery(id+"F14.boolean.opBoolean","COPY",EDGE,{"derivedFrom":makeQuery(id+"F14.opExtrude","SWEPT_EDGE",EDGE,{"disambiguationData":[OSD([sQuery(id+"F13.wireOp",EDGE,"E31.top"),sQuery(id+"F13.wireOp",EDGE,"E31.right")])]})});
            chamfer(context, id + "F23", {"entities" : qUnion([Q0, Q1, Q2, Q3, Q4, Q5, Q6, Q7, Q8, Q9, Q10, Q11, Q12, Q13, Q14, Q15, Q16, Q17, Q18, Q19, Q20, Q21, Q22, Q23, Q24, Q25, Q26, Q27, Q28, Q29, Q30, Q31, Q32, Q33, Q34, Q35]), "width" : 2 * mm, "tangentPropagation" : true});
        }
    });
